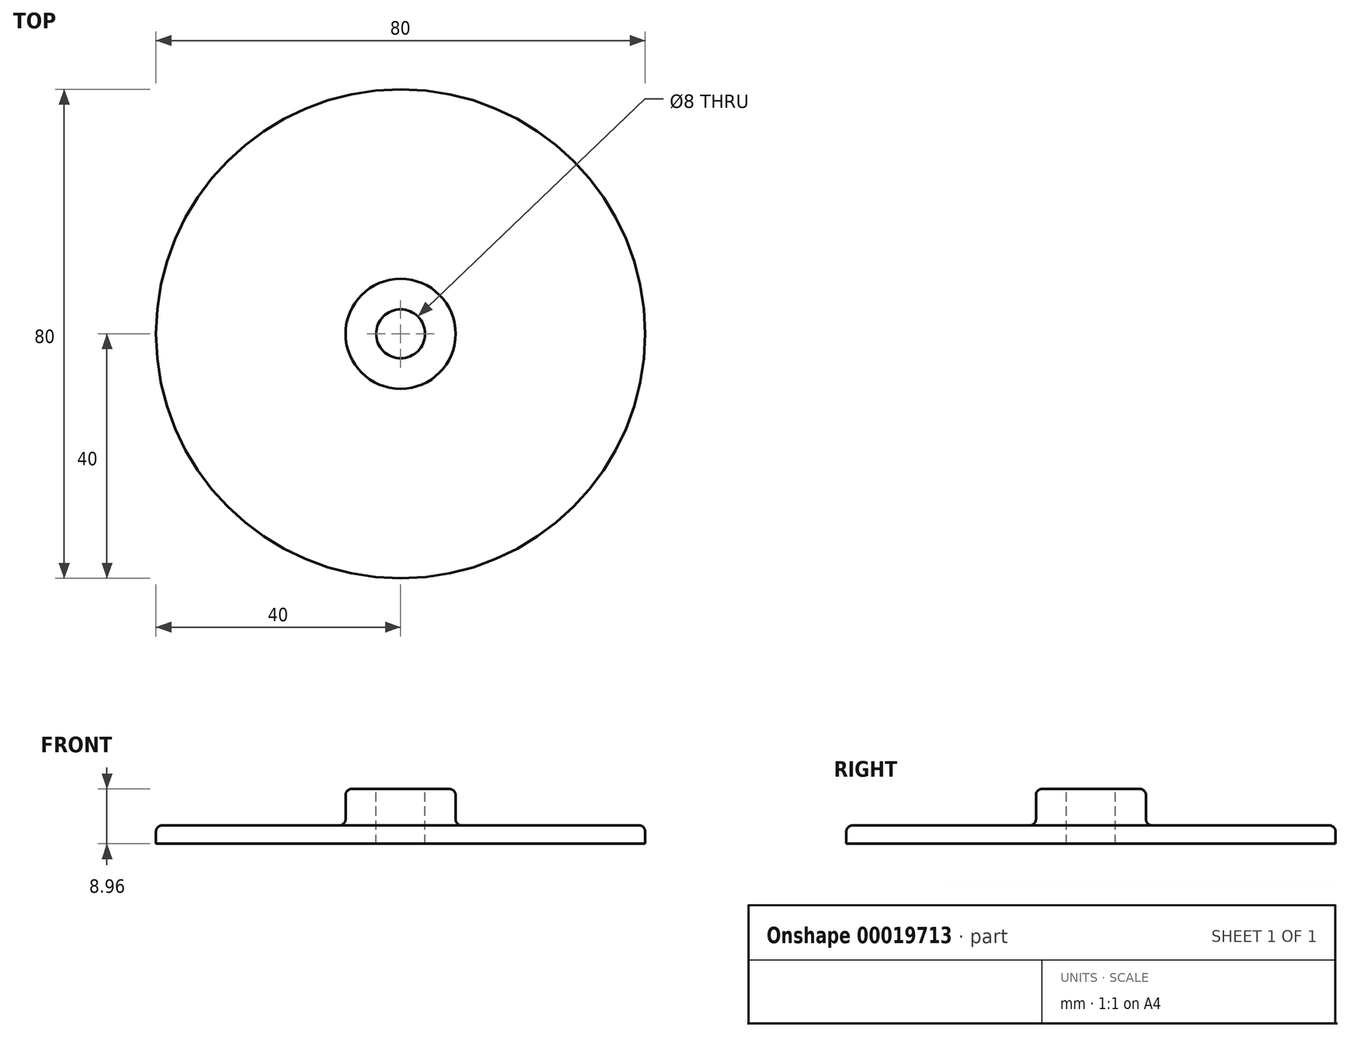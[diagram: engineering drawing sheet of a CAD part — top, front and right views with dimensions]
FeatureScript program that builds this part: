
annotation { "Feature Type Name" : "Feature", "Feature Type Description" : "" }
export const myFeature = defineFeature(function(context is Context, id is Id, definition is map)
    precondition{}
    {
        {
            var Q0;
            Q0=qCreatedBy(makeId("Front.planeOp"),FACE);
            var sketch = newSketch(context, id + "F0", { "sketchPlane" : qUnion([Q0])});
            skLineSegment(sketch, "E0", {"start": v(0, 19.09) * mm, "end": v(0, -18.58) * mm, "construction": true});
            skLineSegment(sketch, "E1", {"start": v(0, 0) * mm, "end": v(52.23, 0) * mm, "construction": true});
            skLineSegment(sketch, "E2", {"start": v(52.23, 0) * mm, "end": v(4, 0) * mm, "construction": true});
            skLineSegment(sketch, "E3", {"start": v(4, 0) * mm, "end": v(4, 8.96) * mm});
            skLineSegment(sketch, "E4", {"start": v(4, 8.96) * mm, "end": v(9, 8.96) * mm});
            skLineSegment(sketch, "E5", {"start": v(9, 8.96) * mm, "end": v(9, 3) * mm});
            skLineSegment(sketch, "E6", {"start": v(9, 3) * mm, "end": v(40, 3) * mm});
            skLineSegment(sketch, "E7", {"start": v(40, 3) * mm, "end": v(40, 0) * mm});
            skLineSegment(sketch, "E8", {"start": v(4, 0) * mm, "end": v(40, 0) * mm});
            skSolve(sketch);
        }
        {
            var Q0;
            Q0 = qSketchRegion(id + "F0", true);
            var Q1;
            Q1=sQuery(id+"F0.wireOp",EDGE,"E0");
            revolve(context, id + "F1", {"entities" : qUnion([Q0]), "axis" : qUnion([Q1]), "revolveType" : RevolveType.FULL});
        }
        {
            var Q0;
            Q0=makeQuery(id+"F1.opRevolve","SWEPT_EDGE",EDGE,{"disambiguationData":[OSD([sQuery(id+"F0.wireOp",EDGE,"E4"),sQuery(id+"F0.wireOp",EDGE,"E5")])]});
            var Q1;
            Q1=makeQuery(id+"F1.opRevolve","SWEPT_EDGE",EDGE,{"disambiguationData":[OSD([sQuery(id+"F0.wireOp",EDGE,"E6"),sQuery(id+"F0.wireOp",EDGE,"E7")])]});
            var Q2;
            Q2=makeQuery(id+"F1.opRevolve","SWEPT_EDGE",EDGE,{"disambiguationData":[OSD([sQuery(id+"F0.wireOp",EDGE,"E5"),sQuery(id+"F0.wireOp",EDGE,"E6")])]});
            fillet(context, id + "F2", {"entities" : qUnion([Q0, Q1, Q2]), "radius" : 1 * mm, "tangentPropagation" : true, "allowEdgeOverflow" : false});
        }
    });
